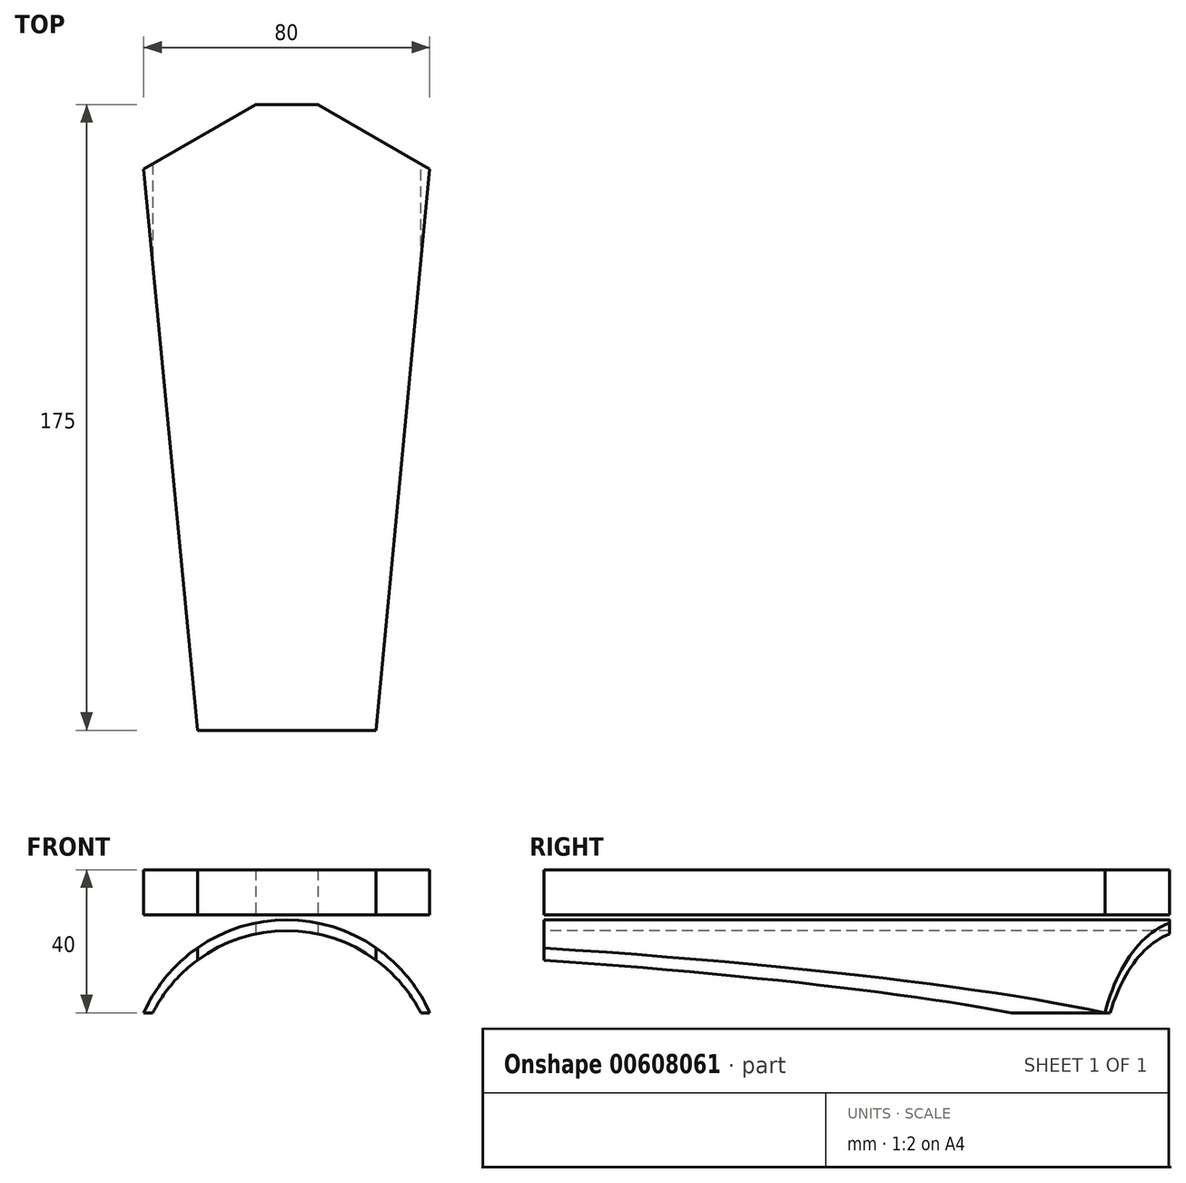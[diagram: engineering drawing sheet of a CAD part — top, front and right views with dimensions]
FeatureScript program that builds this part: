
annotation { "Feature Type Name" : "Feature", "Feature Type Description" : "" }
export const myFeature = defineFeature(function(context is Context, id is Id, definition is map)
    precondition{}
    {
        {
            var Q0;
            Q0=qCreatedBy(makeId("Top.planeOp"),FACE);
            var sketch = newSketch(context, id + "F0", { "sketchPlane" : qUnion([Q0])});
            skLineSegment(sketch, "E0.bottom", {"start": v(40, -90) * mm, "end": v(-40, -90) * mm});
            skLineSegment(sketch, "E0.top", {"start": v(40, 90) * mm, "end": v(-40, 90) * mm});
            skLineSegment(sketch, "E0.left", {"start": v(40, -90) * mm, "end": v(40, 90) * mm});
            skLineSegment(sketch, "E0.right", {"start": v(-40, -90) * mm, "end": v(-40, 90) * mm});
            skPoint(sketch, "E0.middle", {"position": v(0, 0) * mm});
            skLineSegment(sketch, "E1", {"start": v(0, 90) * mm, "end": v(-40, 66.9) * mm});
            skLineSegment(sketch, "E2", {"start": v(0, 90) * mm, "end": v(40, 66.9) * mm});
            skLineSegment(sketch, "E3", {"start": v(-40, 85) * mm, "end": v(40, 85) * mm});
            skSolve(sketch);
        }
        {
            var Q0;
            {var subQ1=sQuery(id+"F0.wireOp",EDGE,"E0.bottom");Q0=makeQuery(id+"F0.imprint","IMPRINT",FACE,{"disambiguationData":[TD([[makeQuery(id+"F0.imprint","IMPRINT",EDGE,{"derivedFrom":subQ1}),-1.0]])]});}
            extrude(context, id + "F1", {"entities" : qUnion([Q0]), "depth" : 40 * mm, "offsetDistance" : 25.4 * mm});
        }
        {
            var Q0;
            Q0=qCreatedBy(makeId("Front.planeOp"),FACE);
            var sketch = newSketch(context, id + "F2", { "sketchPlane" : qUnion([Q0])});
            skArc(sketch, "E4", {"start": v(37.5, 0) * mm, "mid": v(0, 22.93) * mm, "end": v(-37.5, 0) * mm});
            skArc(sketch, "E5", {"start": v(40, 0) * mm, "mid": v(0, 25.99) * mm, "end": v(-40, 0) * mm});
            skLineSegment(sketch, "E6", {"start": v(-37.5, 0) * mm, "end": v(-40, 0) * mm});
            skLineSegment(sketch, "E7", {"start": v(37.5, 0) * mm, "end": v(40, 0) * mm});
            skLineSegment(sketch, "E8.bottom", {"start": v(40, 0) * mm, "end": v(-40, 0) * mm});
            skLineSegment(sketch, "E8.top", {"start": v(40, 27.43) * mm, "end": v(-40, 27.43) * mm});
            skLineSegment(sketch, "E8.left", {"start": v(40, 0) * mm, "end": v(40, 27.43) * mm});
            skLineSegment(sketch, "E8.right", {"start": v(-40, 0) * mm, "end": v(-40, 27.43) * mm});
            skSolve(sketch);
        }
        {
            var Q0;
            {var subQ0=sQuery(id+"F2.wireOp",EDGE,"E4");Q0=makeQuery(id+"F2.imprint","IMPRINT",FACE,{"disambiguationData":[TD([[makeQuery(id+"F2.imprint","IMPRINT",EDGE,{"derivedFrom":subQ0}),1.0]])]});}
            var Q1;
            Q1=makeQuery(id+"F2.imprint","IMPRINT",FACE,{"disambiguationData":[TD([[makeQuery(id+"F2.imprint","IMPRINT",EDGE,{"derivedFrom":sQuery(id+"F2.wireOp",EDGE,"E5")}),-1.0]])]});
            extrude(context, id + "F3", {"entities" : qUnion([Q0, Q1]), "operationType" : NewBodyOperationType.REMOVE, "endBound" : BoundingType.THROUGH_ALL, "oppositeDirection" : true, "depth" : 25.4 * mm, "offsetDistance" : 25.4 * mm});
        }
        {
            var Q0;
            {var subQ0=sQuery(id+"F2.wireOp",EDGE,"E4");Q0=makeQuery(id+"F2.imprint","IMPRINT",FACE,{"disambiguationData":[TD([[makeQuery(id+"F2.imprint","IMPRINT",EDGE,{"derivedFrom":subQ0}),1.0]])]});}
            var Q1;
            Q1=makeQuery(id+"F2.imprint","IMPRINT",FACE,{"disambiguationData":[TD([[makeQuery(id+"F2.imprint","IMPRINT",EDGE,{"derivedFrom":sQuery(id+"F2.wireOp",EDGE,"E5")}),-1.0]])]});
            extrude(context, id + "F4", {"entities" : qUnion([Q0, Q1]), "operationType" : NewBodyOperationType.REMOVE, "endBound" : BoundingType.THROUGH_ALL, "depth" : 25.4 * mm, "offsetDistance" : 25.4 * mm});
        }
        {
            var Q0;
            Q0=makeQuery(id+"F1.opExtrude","CAP_FACE",FACE,{"disambiguationData":[OSD([sQuery(id+"F0.wireOp",EDGE,"E0.bottom"),sQuery(id+"F0.wireOp",EDGE,"E0.left"),sQuery(id+"F0.wireOp",EDGE,"E0.right"),sQuery(id+"F0.wireOp",EDGE,"E1"),sQuery(id+"F0.wireOp",EDGE,"E2"),sQuery(id+"F0.wireOp",EDGE,"E3")])],"isStart":false});
            var sketch = newSketch(context, id + "F5", { "sketchPlane" : qUnion([Q0])});
            skLineSegment(sketch, "E9", {"start": v(-40, 66.9) * mm, "end": v(-25, -90) * mm});
            skLineSegment(sketch, "E10", {"start": v(-25, -90) * mm, "end": v(0, -90) * mm});
            skLineSegment(sketch, "E11", {"start": v(0, -90) * mm, "end": v(25, -90) * mm});
            skLineSegment(sketch, "E12", {"start": v(25, -90) * mm, "end": v(40, 66.9) * mm});
            skSolve(sketch);
        }
        {
            var Q0;
            {var subQ0=sQuery(id+"F5.wireOp",EDGE,"E9");Q0=makeQuery(id+"F5.imprint","IMPRINT",FACE,{"disambiguationData":[TD([[makeQuery(id+"F5.imprint","IMPRINT",EDGE,{"derivedFrom":subQ0}),-1.0]])]});}
            var Q1;
            {var subQ0=sQuery(id+"F5.wireOp",EDGE,"E12");Q1=makeQuery(id+"F5.imprint","IMPRINT",FACE,{"disambiguationData":[TD([[makeQuery(id+"F5.imprint","IMPRINT",EDGE,{"derivedFrom":subQ0}),-1.0]])]});}
            extrude(context, id + "F6", {"entities" : qUnion([Q0, Q1]), "operationType" : NewBodyOperationType.REMOVE, "endBound" : BoundingType.THROUGH_ALL, "oppositeDirection" : true, "depth" : 25.4 * mm, "offsetDistance" : 25.4 * mm});
        }
    });
